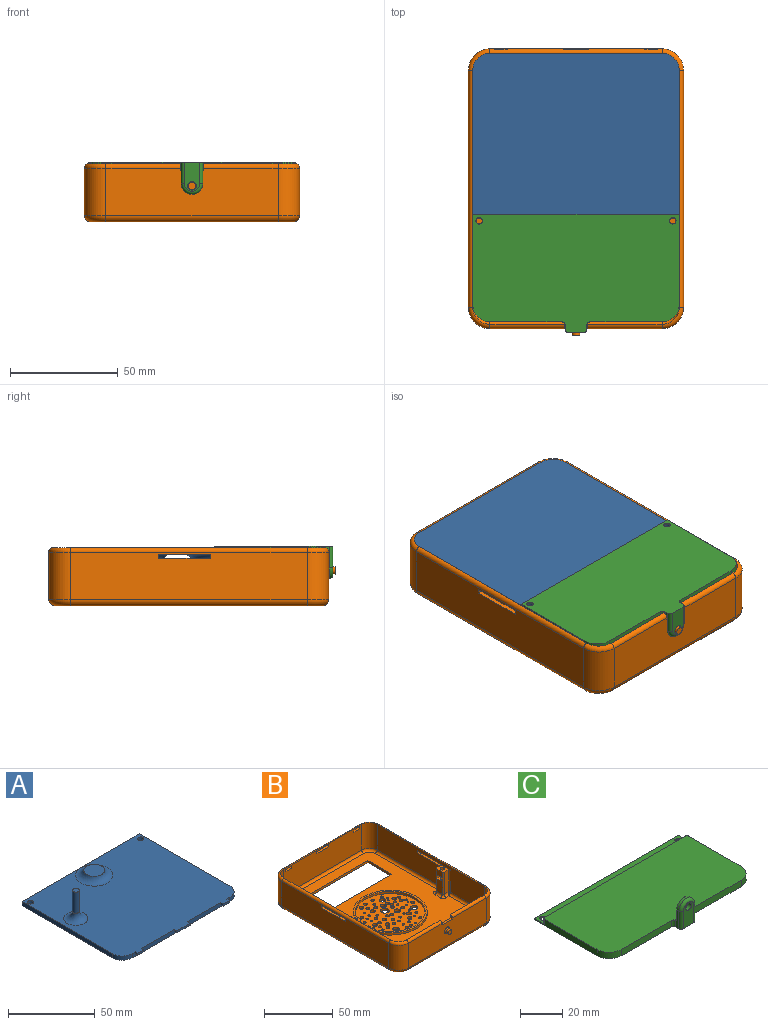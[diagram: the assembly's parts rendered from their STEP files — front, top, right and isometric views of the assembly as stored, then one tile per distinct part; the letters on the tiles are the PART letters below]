
ASSEMBLY  parts=3 mates=2
PART A: 27 faces, bbox 97.4x88.5x23 mm
  f0: plane 2x1.5mm, normal (1,0,0), area 3mm2, adj f14,f16,f18,f26
  f1: plane 2x1.5mm, normal (-1,0,0), area 3mm2, adj f7,f14,f18,f25
  f2: plane 2x1.5mm, normal (1,0,0), area 3mm2, adj f7,f14,f18,f25
  f3: plane 2x1.5mm, normal (-1,0,0), area 3mm2, adj f8,f14,f18,f24
  f4: plane 2x1.5mm, normal (1,0,0), area 3mm2, adj f8,f14,f18,f24
  f5: plane 2x1.5mm, normal (-1,0,0), area 3mm2, adj f14,f16,f18,f26
  f6: plane 96x82mm, normal (0,0,-1), area 7825.3mm2, adj f9,f10,f11,f12,f13,f14,f15,f17
  f7: plane 11x1.5mm, normal (0,-1,0), area 16.5mm2, adj f1,f2,f18,f25
  f8: plane 5x1.5mm, normal (0,-1,0), area 7.5mm2, adj f3,f4,f18,f24
  f9: cylinder r=8mm len=8mm, axis (0,0,-1), area 37.7mm2, adj f6,f10,f14,f18
  f10: plane 74x3mm, normal (1,0,0), area 222mm2, adj f6,f9,f11,f18
  f11: plane 96x3mm, normal (0,1,0), area 288mm2, adj f6,f10,f12,f18
  f12: plane 74x3mm, normal (-1,0,0), area 222mm2, adj f6,f11,f13,f18
  f13: cylinder r=8mm len=8mm, axis (0,0,-1), area 37.7mm2, adj f6,f12,f14,f18
  f14: plane 80x3mm, normal (0,-1,0), area 208.5mm2, adj f0,f1,f2,f3,f4,f5,f6,f9
  f15: cylinder r=1.75mm len=3.5mm, axis (0,0,-1), area 33mm2, adj f6,f18
  f16: plane 5x1.5mm, normal (0,-1,0), area 7.5mm2, adj f0,f5,f18,f26
  f17: cylinder r=1.75mm len=3.5mm, axis (0,0,-1), area 33mm2, adj f6,f18
  f18: plane 96x84mm, normal (0,0,1), area 7349mm2, adj f0,f1,f2,f3,f4,f5,f7,f8
  f19: plane 12x12mm, normal (0,0,1), area 113.1mm2, adj f20
  f20: torus R=10.77mm, axis (0,0,1), area 318.4mm2, adj f18,f19
  f21: cylinder r=2mm len=15mm, axis (0,0,-1), area 188.5mm2, adj f22,f23
  f22: plane 4x4mm, normal (0,0,1), area 12.6mm2, adj f21
  f23: torus R=7mm, axis (0,0,1), area 188.4mm2, adj f18,f21
  f24: plane 5x2mm, normal (0,0,-1), area 10mm2, adj f3,f4,f8,f14
  f25: plane 11x2mm, normal (0,0,-1), area 22mm2, adj f1,f2,f7,f14
  f26: plane 5x2mm, normal (0,0,-1), area 10mm2, adj f0,f5,f14,f16
PART B: 198 faces, bbox 101.6x133.8x27 mm
  f0: plane 80x22mm, normal (0,-1,0), area 1725.7mm2, adj f1,f20,f96,f180,f188,f192,f193,f194
  f1: cylinder r=2mm len=34.75mm, axis (-1,0,0), area 109.2mm2, adj f0,f102,f186,f194
  f2: plane 5.7x5mm, normal (1,0,0), area 28.5mm2, adj f127,f132,f149,f150
  f3: plane 5.7x5mm, normal (-1,0,0), area 28.5mm2, adj f128,f142,f145,f146
  f4: plane 11.5x5.7mm, normal (-1,0,0), area 65.5mm2, adj f140,f145,f146,f164
  f5: cylinder r=1.6mm len=22mm, axis (0,0,-1), area 196mm2, adj f128,f130,f138,f140,f142,f143
  f6: plane 11.3x5.7mm, normal (1,0,0), area 64.4mm2, adj f134,f149,f150,f163
  f7: plane 20x4mm, normal (0,1,0), area 80mm2, adj f128,f144,f145,f160
  f8: plane 20x4mm, normal (0,-1,0), area 80mm2, adj f128,f146,f147,f168
  f9: plane 20x4mm, normal (0,-1,0), area 80mm2, adj f127,f148,f149,f167
  f10: plane 20x4mm, normal (0,1,0), area 80mm2, adj f127,f150,f151,f159
  f11: plane 80x22mm, normal (0,1,0), area 1736mm2, adj f18,f19,f116,f117,f118,f120,f121,f122
  f12: plane 80x23mm, normal (0,-1,0), area 1792mm2, adj f99,f100,f115,f116,f117,f118,f119,f120
  f13: plane 110x22mm, normal (1,0,0), area 2372mm2, adj f18,f96,f107,f108,f109,f110,f176,f184
  f14: plane 110x22mm, normal (-1,0,0), area 2372mm2, adj f19,f20,f111,f112,f113,f114,f183,f191
  f15: plane 110x23mm, normal (1,0,0), area 2288mm2, adj f99,f103,f111,f112,f113,f114,f127,f148
  f16: plane 110x23mm, normal (-1,0,0), area 2288mm2, adj f100,f101,f107,f108,f109,f110,f128,f144
  f17: plane 50.8x50.8mm, normal (0,0,1), area 1631.9mm2, adj f27,f28,f29,f30,f31,f32,f33,f34
  f18: cylinder r=10mm len=22mm, axis (0,0,-1), area 345.6mm2, adj f11,f13,f177,f185
  f19: cylinder r=10mm len=22mm, axis (0,0,-1), area 345.6mm2, adj f11,f14,f181,f189
  f20: cylinder r=10mm len=22mm, axis (0,0,-1), area 345.6mm2, adj f0,f14,f182,f190
  f21: plane 12.2x2mm, normal (0,-1,0), area 24.4mm2, adj f22,f94,f97,f98
  f22: plane 5.7x2mm, normal (-1,0,0), area 11.4mm2, adj f21,f23,f97,f98
  f23: plane 12.2x2mm, normal (0,1,0), area 24.4mm2, adj f22,f94,f97,f98
  f24: plane 24.5x2mm, normal (1,0,0), area 49mm2, adj f25,f95,f97,f98
  f25: plane 72x2mm, normal (0,-1,0), area 144mm2, adj f24,f26,f97,f98
  f26: plane 24.5x2mm, normal (-1,0,0), area 49mm2, adj f25,f95,f97,f98
  f27: cylinder r=1mm len=2mm, axis (0,0,-1), area 12.6mm2, adj f17,f98
  f28: cylinder r=1.85mm len=3.7mm, axis (0,0,-1), area 23.2mm2, adj f17,f98
  f29: cylinder r=2.12mm len=4.25mm, axis (0,0,-1), area 26.7mm2, adj f17,f98
  f30: cylinder r=3.06mm len=6.12mm, axis (0,0,-1), area 38.5mm2, adj f17,f98
  f31: cylinder r=2.36mm len=4.72mm, axis (0,0,-1), area 29.6mm2, adj f17,f98
  f32: cylinder r=1.34mm len=2.68mm, axis (0,0,-1), area 16.8mm2, adj f17,f98
  f33: cylinder r=1.51mm len=3.02mm, axis (0,0,-1), area 19mm2, adj f17,f98
  f34: cylinder r=2.15mm len=4.3mm, axis (0,0,-1), area 27mm2, adj f17,f98
  f35: cylinder r=1.62mm len=3.25mm, axis (0,0,-1), area 20.4mm2, adj f17,f98
  f36: cylinder r=1.17mm len=2.33mm, axis (0,0,-1), area 14.7mm2, adj f17,f98
  f37: cylinder r=0.63mm len=2mm, axis (0,0,-1), area 7.9mm2, adj f17,f98
  f38: cylinder r=0.9mm len=2mm, axis (0,0,-1), area 11.3mm2, adj f17,f98
  f39: cylinder r=1.53mm len=3.05mm, axis (0,0,-1), area 19.2mm2, adj f17,f98
  f40: cylinder r=0.88mm len=2mm, axis (0,0,-1), area 11mm2, adj f17,f98
  f41: cylinder r=1.23mm len=2.46mm, axis (0,0,-1), area 15.4mm2, adj f17,f98
  f42: cylinder r=0.69mm len=2mm, axis (0,0,-1), area 8.7mm2, adj f17,f98
  f43: cylinder r=1.68mm len=3.36mm, axis (0,0,-1), area 21.1mm2, adj f17,f98
  f44: cylinder r=0.8mm len=2mm, axis (0,0,-1), area 10.1mm2, adj f17,f98
  f45: cylinder r=0.78mm len=2mm, axis (0,0,-1), area 9.8mm2, adj f17,f98
  f46: cylinder r=1.7mm len=3.4mm, axis (0,0,-1), area 21.3mm2, adj f17,f98
  f47: cylinder r=0.96mm len=2mm, axis (0,0,-1), area 12mm2, adj f17,f98
  f48: cylinder r=1.19mm len=2.38mm, axis (0,0,-1), area 14.9mm2, adj f17,f98
  f49: cylinder r=0.85mm len=2mm, axis (0,0,-1), area 10.7mm2, adj f17,f98
  f50: cylinder r=1.18mm len=2.37mm, axis (0,0,-1), area 14.9mm2, adj f17,f98
  f51: cylinder r=1.1mm len=2.2mm, axis (0,0,-1), area 13.8mm2, adj f17,f98
  f52: cylinder r=0.95mm len=2mm, axis (0,0,-1), area 11.9mm2, adj f17,f98
  f53: cylinder r=2.62mm len=5.23mm, axis (0,0,-1), area 32.9mm2, adj f17,f98
  f54: cylinder r=1.37mm len=2.74mm, axis (0,0,-1), area 17.2mm2, adj f17,f98
  f55: cylinder r=1.36mm len=2.73mm, axis (0,0,-1), area 17.1mm2, adj f17,f98
  f56: cylinder r=1.22mm len=2.44mm, axis (0,0,-1), area 15.4mm2, adj f17,f98
  f57: cylinder r=1.02mm len=2.04mm, axis (0,0,-1), area 12.8mm2, adj f17,f98
  f58: cylinder r=1.49mm len=2.98mm, axis (0,0,-1), area 18.7mm2, adj f17,f98
  f59: cylinder r=0.89mm len=2mm, axis (0,0,-1), area 11.2mm2, adj f17,f98
  f60: cylinder r=1.46mm len=2.92mm, axis (0,0,-1), area 18.3mm2, adj f17,f98
  f61: cylinder r=0.35mm len=2mm, axis (0,0,-1), area 4.4mm2, adj f17,f98
  f62: cylinder r=1.04mm len=2.07mm, axis (0,0,-1), area 13mm2, adj f17,f98
  f63: cylinder r=1.3mm len=2.6mm, axis (0,0,-1), area 16.3mm2, adj f17,f98
  f64: cylinder r=1.91mm len=3.83mm, axis (0,0,-1), area 24mm2, adj f17,f98
  f65: cylinder r=0.9mm len=2mm, axis (0,0,-1), area 11.3mm2, adj f17,f98
  f66: cylinder r=1.15mm len=2.3mm, axis (0,0,-1), area 14.5mm2, adj f17,f98
  f67: cylinder r=1.96mm len=3.93mm, axis (0,0,-1), area 24.7mm2, adj f17,f98
  f68: cylinder r=0.79mm len=2mm, axis (0,0,-1), area 9.9mm2, adj f17,f98
  f69: cylinder r=1.34mm len=2.69mm, axis (0,0,-1), area 16.9mm2, adj f17,f98
  f70: cylinder r=1.28mm len=2.56mm, axis (0,0,-1), area 16.1mm2, adj f17,f98
  f71: cylinder r=1.46mm len=2.91mm, axis (0,0,-1), area 18.3mm2, adj f17,f98
  f72: cylinder r=1.19mm len=2.38mm, axis (0,0,-1), area 15mm2, adj f17,f98
  f73: cylinder r=1.14mm len=2.28mm, axis (0,0,-1), area 14.3mm2, adj f17,f98
  f74: cylinder r=2.4mm len=4.79mm, axis (0,0,-1), area 30.1mm2, adj f17,f98
  f75: cylinder r=0.94mm len=2mm, axis (0,0,-1), area 11.8mm2, adj f17,f98
  f76: cylinder r=1.35mm len=2.7mm, axis (0,0,-1), area 17mm2, adj f17,f98
  f77: cylinder r=0.96mm len=2mm, axis (0,0,-1), area 12mm2, adj f17,f98
  f78: cylinder r=0.98mm len=2mm, axis (0,0,-1), area 12.3mm2, adj f17,f98
  f79: cylinder r=1.31mm len=2.61mm, axis (0,0,-1), area 16.4mm2, adj f17,f98
  f80: cylinder r=1.09mm len=2.19mm, axis (0,0,-1), area 13.7mm2, adj f17,f98
  f81: cylinder r=1.27mm len=2.54mm, axis (0,0,-1), area 15.9mm2, adj f17,f98
  f82: cylinder r=0.84mm len=2mm, axis (0,0,-1), area 10.6mm2, adj f17,f98
  f83: cylinder r=3.5mm len=7mm, axis (0,0,-1), area 44mm2, adj f97,f98
  f84: cylinder r=1.03mm len=2.06mm, axis (0,0,-1), area 12.9mm2, adj f17,f98
  f85: cylinder r=1.66mm len=3.33mm, axis (0,0,-1), area 20.9mm2, adj f17,f98
  f86: cylinder r=1.3mm len=2.6mm, axis (0,0,-1), area 16.3mm2, adj f17,f98
  f87: cylinder r=1.3mm len=2.59mm, axis (0,0,-1), area 16.3mm2, adj f17,f98
  f88: cylinder r=1.29mm len=2.57mm, axis (0,0,-1), area 16.2mm2, adj f17,f98
  f89: cylinder r=1.12mm len=2.25mm, axis (0,0,-1), area 14.1mm2, adj f17,f98
  f90: cylinder r=1.2mm len=2.41mm, axis (0,0,-1), area 15.1mm2, adj f17,f98
  f91: cylinder r=1.17mm len=2.34mm, axis (0,0,-1), area 14.7mm2, adj f17,f98
  f92: cylinder r=1.09mm len=2.19mm, axis (0,0,-1), area 13.7mm2, adj f17,f98
  f93: cylinder r=2.5mm len=5mm, axis (0,0,-1), area 31.4mm2, adj f97,f98
  f94: plane 5.7x2mm, normal (1,0,0), area 11.4mm2, adj f21,f23,f97,f98
  f95: plane 72x2mm, normal (0,1,0), area 144mm2, adj f24,f26,f97,f98
  f96: cylinder r=10mm len=22mm, axis (0,0,-1), area 345.6mm2, adj f0,f13,f178,f186
  f97: plane 122x92mm, normal (0,0,1), area 6895.5mm2, adj f21,f22,f23,f24,f25,f26,f83,f93
  f98: plane 124x94mm, normal (0,0,-1), area 9327.3mm2, adj f21,f22,f23,f24,f25,f26,f27,f28
  f99: cylinder r=8mm len=23mm, axis (0,0,-1), area 289mm2, adj f12,f15,f153,f189
  f100: cylinder r=8mm len=23mm, axis (0,0,-1), area 289mm2, adj f12,f16,f154,f185
  f101: cylinder r=8mm len=23mm, axis (0,0,-1), area 289mm2, adj f16,f102,f174,f186
  f102: plane 80x23mm, normal (0,1,0), area 1808.5mm2, adj f1,f101,f103,f175,f188,f192,f193,f194
  f103: cylinder r=8mm len=23mm, axis (0,0,-1), area 289mm2, adj f15,f102,f173,f190
  f104: cylinder r=25.4mm len=50.8mm, axis (0,0,-1), area 319.2mm2, adj f17,f106
  f105: cylinder r=26.9mm len=53.8mm, axis (0,0,-1), area 338mm2, adj f97,f106
  f106: plane 53.8x53.8mm, normal (0,0,1), area 246.5mm2, adj f104,f105
  f107: plane 24x2mm, normal (0,0,-1), area 48mm2, adj f13,f16,f108,f110
  f108: plane 2x2mm, normal (0,1,0), area 4mm2, adj f13,f16,f107,f109
  f109: plane 24x2mm, normal (0,0,1), area 48mm2, adj f13,f16,f108,f110
  f110: plane 2x2mm, normal (0,-1,0), area 4mm2, adj f13,f16,f107,f109
  f111: plane 2x2mm, normal (0,-1,0), area 4mm2, adj f14,f15,f112,f114
  f112: plane 24x2mm, normal (0,0,1), area 48mm2, adj f14,f15,f111,f113
  f113: plane 2x2mm, normal (0,1,0), area 4mm2, adj f14,f15,f112,f114
  f114: plane 24x2mm, normal (0,0,-1), area 48mm2, adj f14,f15,f111,f113
  f115: plane 12x1.73mm, normal (0,0,-1), area 20.8mm2, adj f12,f116,f118,f187
  f116: plane 2x2mm, normal (-1,0,0), area 3.9mm2, adj f11,f12,f115,f117,f187
  f117: plane 12x2mm, normal (0,0,1), area 24mm2, adj f11,f12,f116,f118
  f118: plane 2x2mm, normal (1,0,0), area 3.9mm2, adj f11,f12,f115,f117,f187
  f119: plane 6x1.73mm, normal (0,0,-1), area 10.4mm2, adj f12,f120,f122,f187
  f120: plane 2x2mm, normal (-1,0,0), area 3.9mm2, adj f11,f12,f119,f121,f187
  f121: plane 6x2mm, normal (0,0,1), area 12mm2, adj f11,f12,f120,f122
  f122: plane 2x2mm, normal (1,0,0), area 3.9mm2, adj f11,f12,f119,f121,f187
  f123: plane 6x1.73mm, normal (0,0,-1), area 10.4mm2, adj f12,f124,f126,f187
  f124: plane 2x2mm, normal (-1,0,0), area 3.9mm2, adj f11,f12,f123,f125,f187
  f125: plane 6x2mm, normal (0,0,1), area 12mm2, adj f11,f12,f124,f126
  f126: plane 2x2mm, normal (1,0,0), area 3.9mm2, adj f11,f12,f123,f125,f187
  f127: plane 9.7x6mm, normal (0,0,1), area 38.2mm2, adj f2,f9,f10,f15,f129,f148,f149,f150
  f128: plane 9.7x6mm, normal (0,0,1), area 38.2mm2, adj f3,f5,f7,f8,f16,f144,f145,f146
  f129: cylinder r=1.6mm len=5mm, axis (0,0,-1), area 50.3mm2, adj f127,f132
  f130: plane 3.2x3.2mm, normal (0,0,1), area 8mm2, adj f5
  f131: plane 5x3.7mm, normal (0,-1,0), area 18.5mm2, adj f132,f134,f135,f150
  f132: plane 5.7x5mm, normal (0,0,-1), area 20.5mm2, adj f2,f129,f131,f133,f135
  f133: plane 5x3.7mm, normal (0,1,0), area 18.5mm2, adj f132,f134,f135,f149
  f134: plane 5.7x5mm, normal (0,0,1), area 20.5mm2, adj f6,f131,f133,f135,f137
  f135: plane 5.7x3.7mm, normal (1,0,0), area 21.1mm2, adj f131,f132,f133,f134
  f136: plane 3.2x3.2mm, normal (0,0,1), area 8mm2, adj f137
  f137: cylinder r=1.6mm len=13.3mm, axis (0,0,-1), area 133.7mm2, adj f134,f136
  f138: plane 3.5x1.6mm, normal (-1,0,0), area 5.6mm2, adj f5,f139,f140,f142
  f139: plane 4x3.5mm, normal (0,-1,0), area 14mm2, adj f138,f140,f142,f145
  f140: plane 5.9x4mm, normal (0,0,1), area 16.6mm2, adj f4,f5,f138,f139,f141,f143,f146
  f141: plane 3.98x3.5mm, normal (0,1,0), area 13.9mm2, adj f140,f142,f143,f146
  f142: plane 5.9x4mm, normal (0,0,-1), area 16.6mm2, adj f3,f5,f138,f139,f141,f143,f146
  f143: plane 3.5x1.8mm, normal (-1,0,0), area 6.3mm2, adj f5,f140,f141,f142
  f144: cylinder r=1mm len=20mm, axis (0,0,1), area 31.4mm2, adj f7,f16,f128,f158
  f145: cylinder r=1mm len=20mm, axis (0,0,-1), area 31.4mm2, adj f3,f4,f7,f128,f139,f162
  f146: cylinder r=1mm len=20mm, axis (0,0,1), area 30.7mm2, adj f3,f4,f8,f128,f140,f141,f142,f166
  f147: cylinder r=1mm len=20mm, axis (0,0,-1), area 31.4mm2, adj f8,f16,f128,f170
  f148: cylinder r=1mm len=20mm, axis (0,0,-1), area 31.4mm2, adj f9,f15,f127,f169
  f149: cylinder r=1mm len=20mm, axis (0,0,1), area 31.4mm2, adj f2,f6,f9,f127,f133,f165
  f150: cylinder r=1mm len=20mm, axis (0,0,-1), area 31.4mm2, adj f2,f6,f10,f127,f131,f161
  f151: cylinder r=1mm len=20mm, axis (0,0,1), area 31.4mm2, adj f10,f15,f127,f157
  f152: cylinder r=2mm len=80mm, axis (1,0,0), area 251.3mm2, adj f12,f97,f153,f154
  f153: torus R=6mm, axis (0,0,1), area 35.9mm2, adj f97,f99,f152,f155
  f154: torus R=6mm, axis (0,0,1), area 35.9mm2, adj f97,f100,f152,f156
  f155: cylinder r=2mm len=65.3mm, axis (0,1,0), area 204mm2, adj f15,f97,f153,f157
  f156: cylinder r=2mm len=65.3mm, axis (0,-1,0), area 204mm2, adj f16,f97,f154,f158
  f157: bspline ~2.39x2mm, area 3.3mm2, adj f151,f155,f159
  f158: bspline ~2.39x2mm, area 3.3mm2, adj f144,f156,f160
  f159: cylinder r=2mm len=4mm, axis (-1,0,0), area 11.4mm2, adj f10,f97,f157,f161
  f160: cylinder r=2mm len=4mm, axis (-1,0,0), area 11.4mm2, adj f7,f97,f158,f162
  f161: torus R=3mm, axis (0,0,1), area 8.5mm2, adj f97,f150,f159,f163
  f162: torus R=3mm, axis (0,0,1), area 8.5mm2, adj f97,f145,f160,f164
  f163: cylinder r=2mm len=5.7mm, axis (0,1,0), area 17.9mm2, adj f6,f97,f161,f165
  f164: cylinder r=2mm len=5.7mm, axis (0,-1,0), area 17.9mm2, adj f4,f97,f162,f166
  f165: torus R=3mm, axis (0,0,1), area 8.5mm2, adj f97,f149,f163,f167
  f166: torus R=3mm, axis (0,0,1), area 8.5mm2, adj f97,f146,f164,f168
  f167: cylinder r=2mm len=4mm, axis (1,0,0), area 11.4mm2, adj f9,f97,f165,f169
  f168: cylinder r=2mm len=4mm, axis (1,0,0), area 11.4mm2, adj f8,f97,f166,f170
  f169: bspline ~2.39x2mm, area 3.3mm2, adj f148,f167,f171
  f170: bspline ~2.39x2mm, area 3.3mm2, adj f147,f168,f172
  f171: cylinder r=2mm len=35mm, axis (0,1,0), area 108.8mm2, adj f15,f97,f169,f173
  f172: cylinder r=2mm len=35mm, axis (0,-1,0), area 108.8mm2, adj f16,f97,f170,f174
  f173: torus R=6mm, axis (0,0,1), area 35.9mm2, adj f97,f103,f171,f175
  f174: torus R=6mm, axis (0,0,1), area 35.9mm2, adj f97,f101,f172,f175
  f175: cylinder r=2mm len=80mm, axis (-1,0,0), area 251.3mm2, adj f97,f102,f173,f174
  f176: cylinder r=3mm len=110mm, axis (0,1,0), area 518.4mm2, adj f13,f98,f177,f178
  f177: torus R=7mm, axis (0,0,1), area 66mm2, adj f18,f98,f176,f179
  f178: torus R=7mm, axis (0,0,1), area 66mm2, adj f96,f98,f176,f180
  f179: cylinder r=3mm len=80mm, axis (-1,0,0), area 377mm2, adj f11,f98,f177,f181
  f180: cylinder r=3mm len=80mm, axis (1,0,0), area 377mm2, adj f0,f98,f178,f182
  f181: torus R=7mm, axis (0,0,1), area 66mm2, adj f19,f98,f179,f183
  f182: torus R=7mm, axis (0,0,1), area 66mm2, adj f20,f98,f180,f183
  f183: cylinder r=3mm len=110mm, axis (0,-1,0), area 518.4mm2, adj f14,f98,f181,f182
  f184: cylinder r=2mm len=110mm, axis (0,-1,0), area 345.6mm2, adj f13,f16,f185,f186
  f185: torus R=8mm, axis (0,0,1), area 45.8mm2, adj f18,f100,f184,f187
  f186: torus R=8mm, axis (0,0,1), area 45.8mm2, adj f1,f96,f101,f184
  f187: cylinder r=2mm len=80mm, axis (1,0,0), area 226.2mm2, adj f11,f12,f115,f116,f118,f119,f120,f122
  f188: cylinder r=2mm len=34.75mm, axis (-1,0,0), area 109.2mm2, adj f0,f102,f190,f192
  f189: torus R=8mm, axis (0,0,1), area 45.8mm2, adj f19,f99,f187,f191
  f190: torus R=8mm, axis (0,0,1), area 45.8mm2, adj f20,f103,f188,f191
  f191: cylinder r=2mm len=110mm, axis (0,1,0), area 345.6mm2, adj f14,f15,f189,f190
  f192: plane 3x2mm, normal (1,0,0), area 5.1mm2, adj f0,f102,f188,f193
  f193: plane 10.5x2mm, normal (0,0,1), area 21mm2, adj f0,f102,f192,f194
  f194: plane 3x2mm, normal (-1,0,0), area 5.1mm2, adj f0,f1,f102,f193
  f195: cylinder r=1.75mm len=3.5mm, axis (0,1,0), area 22mm2, adj f196,f197
  f196: plane 3.5x3.5mm, normal (0,-1,0), area 9.6mm2, adj f195
  f197: torus R=2.75mm, axis (0,1,0), area 20.9mm2, adj f0,f195
PART C: 28 faces, bbox 96x55x15.4 mm
  f0: cylinder r=2mm len=4mm, axis (0,-1,0), area 30.2mm2, adj f13,f26
  f1: cylinder r=5mm len=10mm, axis (0,1,0), area 23.6mm2, adj f11,f12,f15,f23
  f2: plane 33.5x3.7mm, normal (0,-1,0), area 124mm2, adj f8,f10,f18,f24
  f3: plane 96x7mm, normal (0,0,1), area 562.3mm2, adj f4,f5,f7,f9,f19,f20,f21,f22
  f4: plane 96x0.7mm, normal (0,1,0), area 67.2mm2, adj f3,f5,f7,f8
  f5: plane 42x3.7mm, normal (-1,0,0), area 134.4mm2, adj f3,f4,f8,f10,f19,f24
  f6: plane 33.5x3.7mm, normal (0,-1,0), area 124mm2, adj f8,f10,f17,f25
  f7: plane 42x3.7mm, normal (1,0,0), area 134.4mm2, adj f3,f4,f8,f10,f20,f25
  f8: plane 96x55mm, normal (0,0,-1), area 4808.4mm2, adj f2,f4,f5,f6,f7,f11,f12,f13
  f9: plane 94x3mm, normal (0,1,0), area 282mm2, adj f3,f10,f19,f20
  f10: plane 96x45mm, normal (0,0,1), area 4207mm2, adj f2,f5,f6,f7,f9,f17,f18,f19
  f11: plane 10x2mm, normal (-1,0,0), area 17mm2, adj f1,f8,f16,f18,f23,f27
  f12: plane 10x2mm, normal (1,0,0), area 17mm2, adj f1,f8,f14,f17,f23,f27
  f13: plane 13.5x7mm, normal (0,-1,0), area 76.7mm2, adj f0,f8,f14,f15,f16
  f14: cylinder r=1.5mm len=10mm, axis (0,0,-1), area 23.6mm2, adj f8,f12,f13,f15
  f15: torus R=3.5mm, axis (0,-1,0), area 33mm2, adj f1,f13,f14,f16
  f16: cylinder r=1.5mm len=10mm, axis (0,0,1), area 23.6mm2, adj f8,f11,f13,f15
  f17: cylinder r=1.5mm len=3.83mm, axis (0,0,-1), area 8.7mm2, adj f6,f8,f10,f12,f27
  f18: cylinder r=1.5mm len=3.83mm, axis (0,0,1), area 8.7mm2, adj f2,f8,f10,f11,f27
  f19: cylinder r=1mm len=3mm, axis (0,0,1), area 4.7mm2, adj f3,f5,f9,f10
  f20: cylinder r=1mm len=3mm, axis (0,0,-1), area 4.7mm2, adj f3,f7,f9,f10
  f21: cylinder r=1.5mm len=3mm, axis (0,0,1), area 6.6mm2, adj f3,f8
  f22: cylinder r=1.5mm len=3mm, axis (0,0,1), area 6.6mm2, adj f3,f8
  f23: plane 10.3x10mm, normal (0,1,0), area 71mm2, adj f1,f11,f12,f26,f27
  f24: cylinder r=8mm len=8mm, axis (0,0,-1), area 46.5mm2, adj f2,f5,f8,f10
  f25: cylinder r=8mm len=8mm, axis (0,0,1), area 46.5mm2, adj f6,f7,f8,f10
  f26: cone r=2.6mm half-angle=45deg, axis (0,1,0), area 12.3mm2, adj f0,f23
  f27: cylinder r=1mm len=10.17mm, axis (1,0,0), area 15.7mm2, adj f10,f11,f12,f17,f18,f23
PLACE A rot(axis=(1,0,0),180deg) t=(0,-7,27)mm
PLACE B at identity fixed
PLACE C rot(axis=(0,1,0),180deg) t=(0,-56.9,27.7)mm
MATE fastened B.f11 <-> A.f7  axis (0,1,0) through (0,70,24)mm
MATE fastened C.f22 <-> A.f15  axis (0,0,-1) through (45,-9.9,27)mm
